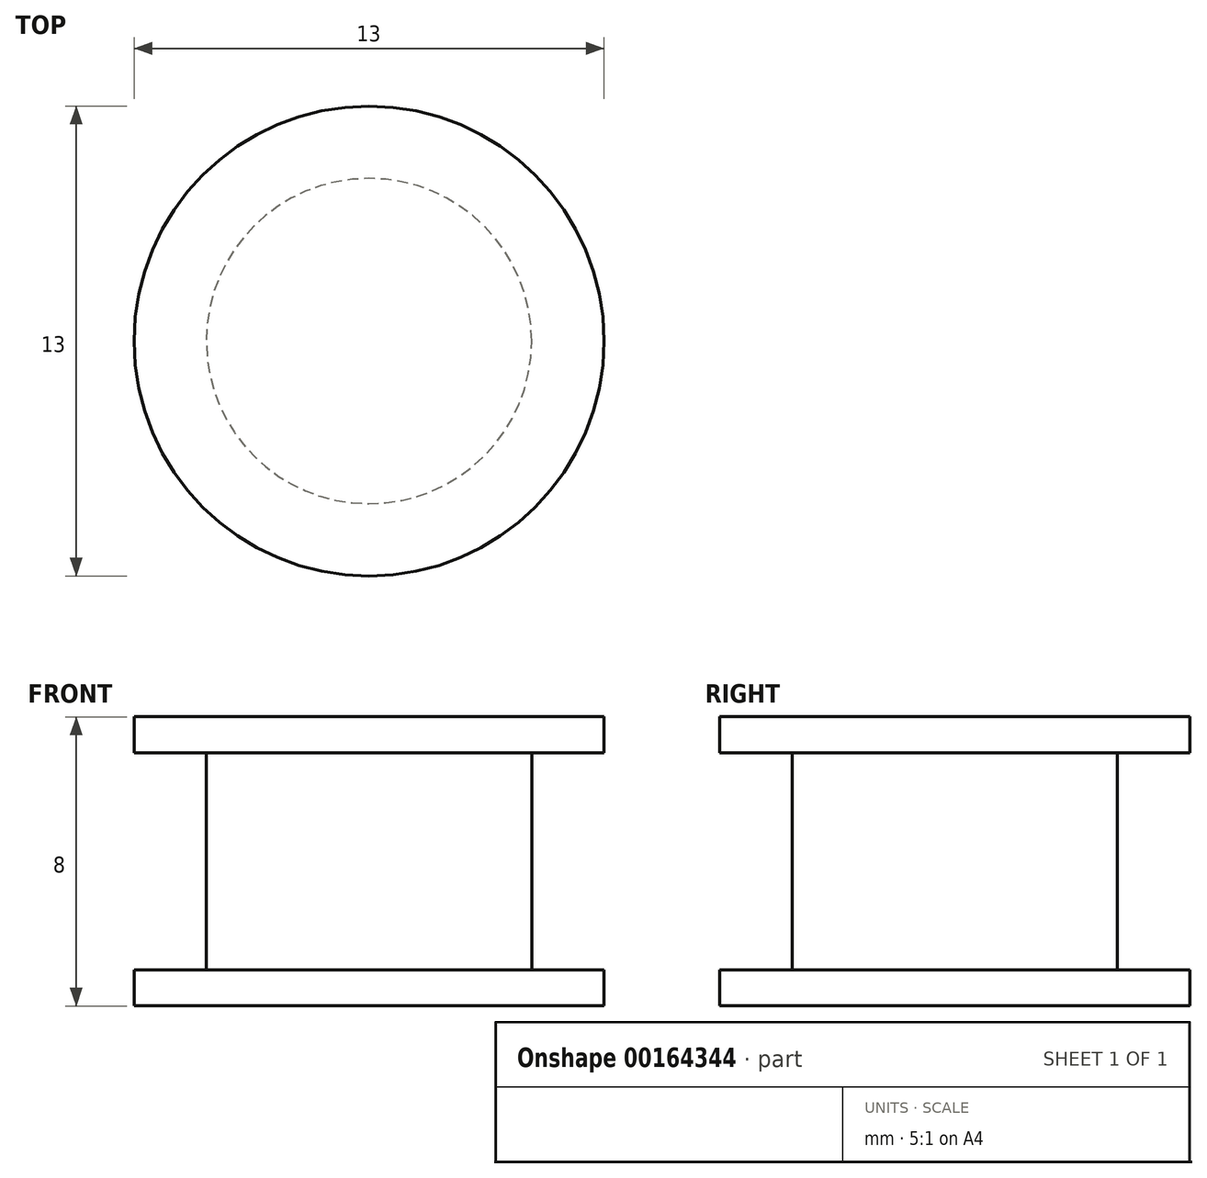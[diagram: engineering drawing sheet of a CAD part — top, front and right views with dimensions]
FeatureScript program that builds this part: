
annotation { "Feature Type Name" : "Feature", "Feature Type Description" : "" }
export const myFeature = defineFeature(function(context is Context, id is Id, definition is map)
    precondition{}
    {
        {
            var Q0;
            Q0=qCreatedBy(makeId("Front.planeOp"),FACE);
            var sketch = newSketch(context, id + "F0", { "sketchPlane" : qUnion([Q0])});
            skLineSegment(sketch, "E0", {"start": v(0, 13.26) * mm, "end": v(6.5, 13.26) * mm});
            skLineSegment(sketch, "E1", {"start": v(6.5, 13.26) * mm, "end": v(6.5, 12.26) * mm});
            skLineSegment(sketch, "E2", {"start": v(6.5, 12.26) * mm, "end": v(4.5, 12.26) * mm});
            skLineSegment(sketch, "E3", {"start": v(4.5, 12.26) * mm, "end": v(4.5, 6.26) * mm});
            skLineSegment(sketch, "E4", {"start": v(4.5, 6.26) * mm, "end": v(6.5, 6.26) * mm});
            skLineSegment(sketch, "E5", {"start": v(6.5, 6.26) * mm, "end": v(6.5, 5.26) * mm});
            skLineSegment(sketch, "E6", {"start": v(6.5, 5.26) * mm, "end": v(0, 5.26) * mm});
            skLineSegment(sketch, "E7", {"start": v(0, 0) * mm, "end": v(0, 3.64) * mm, "construction": true});
            skLineSegment(sketch, "E8", {"start": v(0, 5.26) * mm, "end": v(0, 13.26) * mm});
            skSolve(sketch);
        }
        {
            var Q0;
            Q0 = qSketchRegion(id + "F0", true);
            var Q1;
            Q1=sQuery(id+"F0.wireOp",EDGE,"E7");
            revolve(context, id + "F1", {"entities" : qUnion([Q0]), "axis" : qUnion([Q1]), "revolveType" : RevolveType.FULL});
        }
    });
